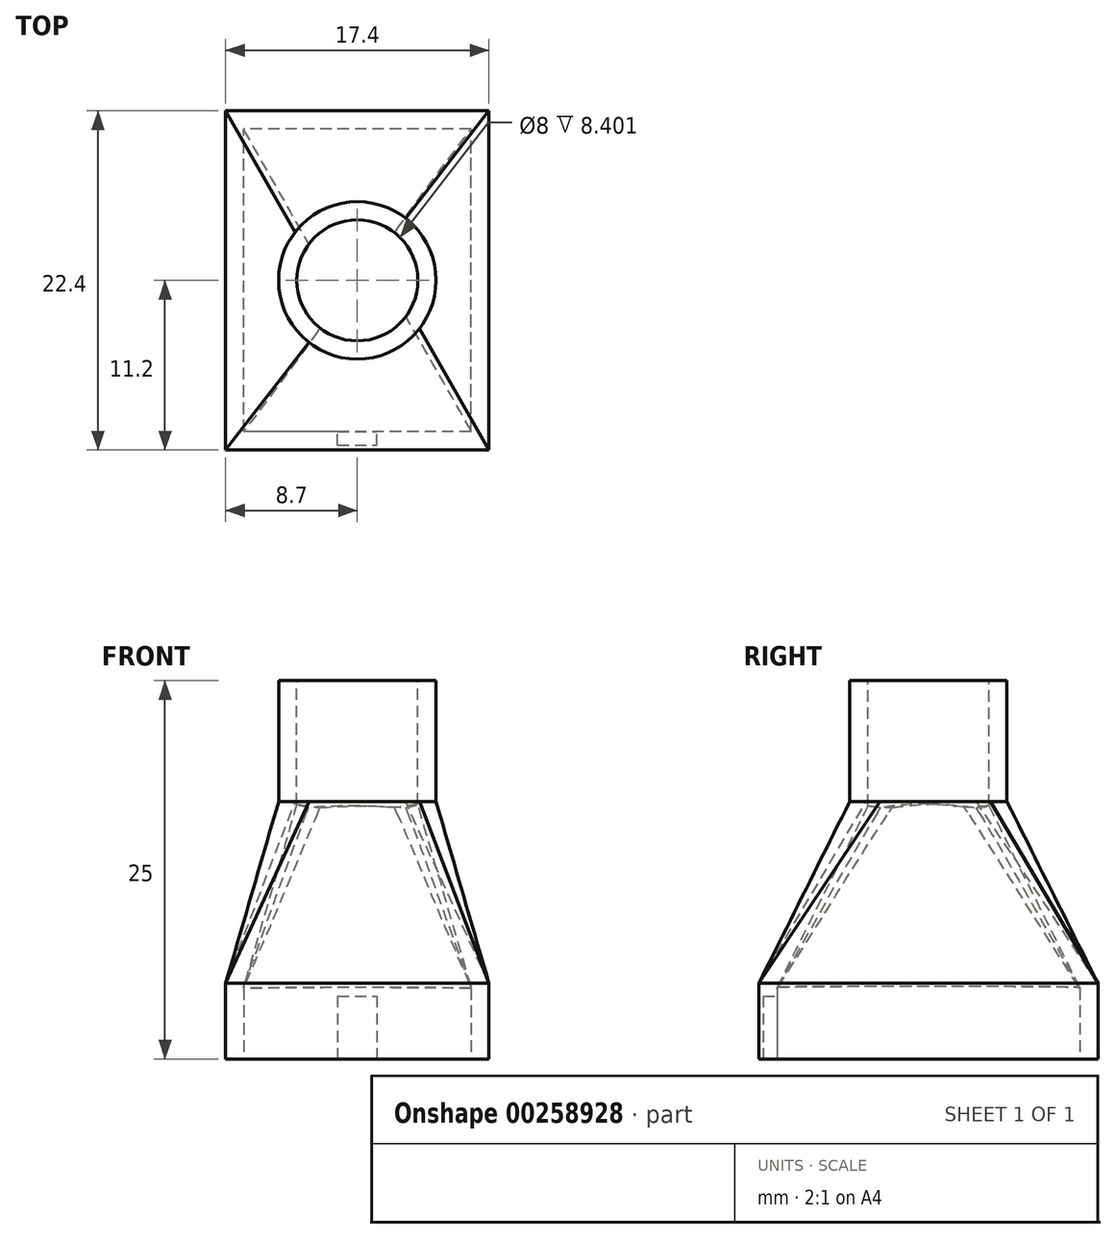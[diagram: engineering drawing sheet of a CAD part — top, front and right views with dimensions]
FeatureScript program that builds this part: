
annotation { "Feature Type Name" : "Feature", "Feature Type Description" : "" }
export const myFeature = defineFeature(function(context is Context, id is Id, definition is map)
    precondition{}
    {
        {
            var Q0;
            Q0=qCreatedBy(makeId("Top.planeOp"),FACE);
            var sketch = newSketch(context, id + "F0", { "sketchPlane" : qUnion([Q0])});
            skLineSegment(sketch, "E0.bottom", {"start": v(7.5, -10) * mm, "end": v(-7.5, -10) * mm});
            skLineSegment(sketch, "E0.top", {"start": v(7.5, 10) * mm, "end": v(-7.5, 10) * mm});
            skLineSegment(sketch, "E0.left", {"start": v(7.5, -10) * mm, "end": v(7.5, 10) * mm});
            skLineSegment(sketch, "E0.right", {"start": v(-7.5, -10) * mm, "end": v(-7.5, 10) * mm});
            skPoint(sketch, "E0.middle", {"position": v(0, 0) * mm});
            skLineSegment(sketch, "E1.0", {"start": v(8.7, 11.2) * mm, "end": v(-8.7, 11.2) * mm});
            skLineSegment(sketch, "E1.1", {"start": v(8.7, -11.2) * mm, "end": v(8.7, 11.2) * mm});
            skLineSegment(sketch, "E1.2", {"start": v(8.7, -11.2) * mm, "end": v(-8.7, -11.2) * mm});
            skLineSegment(sketch, "E1.3", {"start": v(-8.7, -11.2) * mm, "end": v(-8.7, 11.2) * mm});
            skSolve(sketch);
        }
        {
            var Q0;
            Q0=qCreatedBy(makeId("Top.planeOp"),FACE);
            cPlane(context, id + "F1", {"entities" : qUnion([Q0]), "cplaneType" : CPlaneType.OFFSET, "offset" : 25 * mm, "width" : 150 * mm, "height" : 150 * mm});
        }
        {
            var Q0;
            Q0=qCreatedBy(id+"F1.planeOp",FACE);
            var sketch = newSketch(context, id + "F2", { "sketchPlane" : qUnion([Q0])});
            skCircle(sketch, "E2", {"center": v(0, 0) * mm, "radius": 4 * mm});
            skCircle(sketch, "E3", {"center": v(0, 0) * mm, "radius": 5.2 * mm});
            skSolve(sketch);
        }
        {
            var Q0;
            Q0=makeQuery(id+"F2.imprint","IMPRINT",FACE,{"disambiguationData":[TD([[makeQuery(id+"F2.imprint","IMPRINT",EDGE,{"derivedFrom":sQuery(id+"F2.wireOp",EDGE,"E2")}),-1.0]])]});
            var Q1;
            Q1=makeQuery(id+"F2.imprint","IMPRINT",FACE,{"disambiguationData":[TD([[makeQuery(id+"F2.imprint","IMPRINT",EDGE,{"derivedFrom":sQuery(id+"F2.wireOp",EDGE,"E2")}),1.0]])]});
            extrude(context, id + "F3", {"entities" : qUnion([Q0, Q1]), "oppositeDirection" : true, "depth" : 8 * mm});
        }
        {
            var Q0;
            Q0=makeQuery(id+"F0.imprint","IMPRINT",FACE,{"disambiguationData":[TD([[makeQuery(id+"F0.imprint","IMPRINT",EDGE,{"derivedFrom":sQuery(id+"F0.wireOp",EDGE,"E0.bottom")}),1.0]])]});
            var Q1;
            Q1=makeQuery(id+"F0.imprint","IMPRINT",FACE,{"disambiguationData":[TD([[makeQuery(id+"F0.imprint","IMPRINT",EDGE,{"derivedFrom":sQuery(id+"F0.wireOp",EDGE,"E0.bottom")}),-1.0]])]});
            extrude(context, id + "F4", {"entities" : qUnion([Q0, Q1]), "depth" : 5 * mm});
        }
        {
            var Q1;
            Q1=makeQuery(id+"F4.opExtrude","CAP_FACE",FACE,{"disambiguationData":[OSD([sQuery(id+"F0.wireOp",EDGE,"E1.0"),sQuery(id+"F0.wireOp",EDGE,"E1.1"),sQuery(id+"F0.wireOp",EDGE,"E1.2"),sQuery(id+"F0.wireOp",EDGE,"E1.3")])],"isStart":false});
            var Q2;
            Q2=makeQuery(id+"F3.opExtrude","CAP_FACE",FACE,{"disambiguationData":[OSD([sQuery(id+"F2.wireOp",EDGE,"E3")])],"isStart":false});
            loft(context, id + "F5", {"operationType" : NewBodyOperationType.ADD, "sheetProfilesArray" : [{ "sheetProfileEntities" : qUnion([Q1]) }, { "sheetProfileEntities" : qUnion([Q2]) }]});
        }
        {
            var Q0;
            Q0=makeQuery(id+"F4.opExtrude","CAP_FACE",FACE,{"disambiguationData":[OSD([sQuery(id+"F0.wireOp",EDGE,"E1.0"),sQuery(id+"F0.wireOp",EDGE,"E1.1"),sQuery(id+"F0.wireOp",EDGE,"E1.2"),sQuery(id+"F0.wireOp",EDGE,"E1.3")])],"isStart":true});
            var Q1;
            Q1=makeQuery(id+"F3.opExtrude","CAP_FACE",FACE,{"disambiguationData":[OSD([sQuery(id+"F2.wireOp",EDGE,"E3")])],"isStart":true});
            shell(context, id + "F6", {"entities" : qUnion([Q0, Q1]), "thickness" : 1.2 * mm});
        }
        {
            var Q0;
            Q0=makeQuery(id+"F4.opExtrude","CAP_FACE",FACE,{"disambiguationData":[OSD([sQuery(id+"F0.wireOp",EDGE,"E1.0"),sQuery(id+"F0.wireOp",EDGE,"E1.1"),sQuery(id+"F0.wireOp",EDGE,"E1.2"),sQuery(id+"F0.wireOp",EDGE,"E1.3")])],"isStart":true});
            var sketch = newSketch(context, id + "F7", { "sketchPlane" : qUnion([Q0])});
            skLineSegment(sketch, "E4.bottom", {"start": v(-1.3, 10.9) * mm, "end": v(1.3, 10.9) * mm});
            skLineSegment(sketch, "E4.top", {"start": v(-1.3, 9.1) * mm, "end": v(1.3, 9.1) * mm});
            skLineSegment(sketch, "E4.left", {"start": v(-1.3, 10.9) * mm, "end": v(-1.3, 9.1) * mm});
            skLineSegment(sketch, "E4.right", {"start": v(1.3, 10.9) * mm, "end": v(1.3, 9.1) * mm});
            skPoint(sketch, "E4.middle", {"position": v(0, 10) * mm});
            skSolve(sketch);
        }
        {
            var Q0;
            {var subQ0=sQuery(id+"F7.wireOp",EDGE,"E4.bottom");Q0=makeQuery(id+"F7.imprint","IMPRINT",FACE,{"disambiguationData":[TD([[makeQuery(id+"F7.imprint","IMPRINT",EDGE,{"derivedFrom":subQ0}),-1.0]])]});}
            var Q1;
            {var subQ0=sQuery(id+"F7.wireOp",EDGE,"E4.top");Q1=makeQuery(id+"F7.imprint","IMPRINT",FACE,{"disambiguationData":[TD([[makeQuery(id+"F7.imprint","IMPRINT",EDGE,{"derivedFrom":subQ0}),1.0]])]});}
            extrude(context, id + "F8", {"entities" : qUnion([Q0, Q1]), "operationType" : NewBodyOperationType.REMOVE, "oppositeDirection" : true, "depth" : 4.16 * mm});
        }
    });
